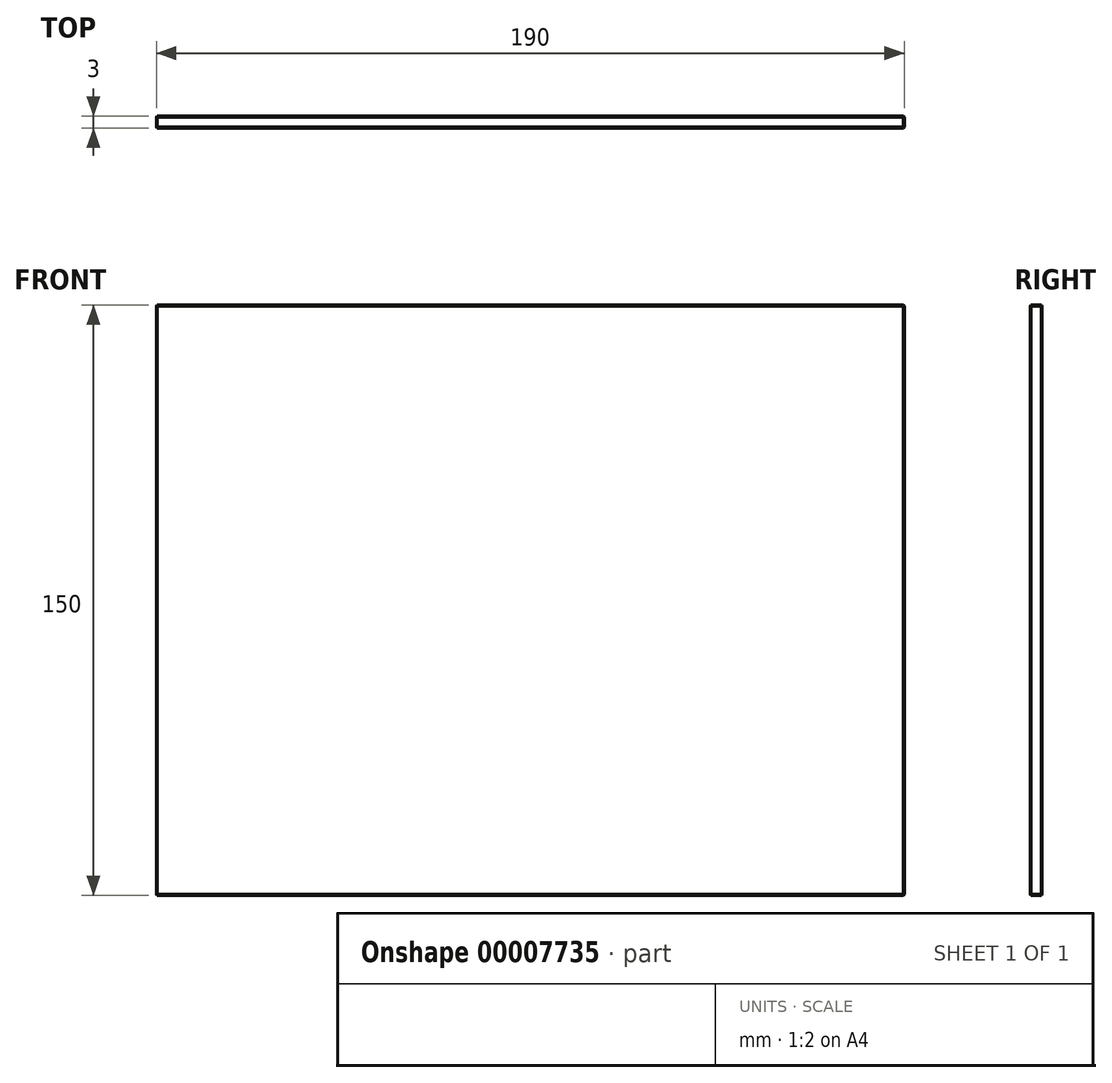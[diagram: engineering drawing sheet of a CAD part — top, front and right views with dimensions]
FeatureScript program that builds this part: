
annotation { "Feature Type Name" : "Feature", "Feature Type Description" : "" }
export const myFeature = defineFeature(function(context is Context, id is Id, definition is map)
    precondition{}
    {
        {
            var Q0;
            Q0=qCreatedBy(makeId("Front.planeOp"),FACE);
            var sketch = newSketch(context, id + "F0", { "sketchPlane" : qUnion([Q0])});
            skLineSegment(sketch, "E0.bottom", {"start": v(0, 0) * mm, "end": v(190, 0) * mm});
            skLineSegment(sketch, "E0.top", {"start": v(0, 150) * mm, "end": v(190, 150) * mm});
            skLineSegment(sketch, "E0.left", {"start": v(0, 0) * mm, "end": v(0, 150) * mm});
            skLineSegment(sketch, "E0.right", {"start": v(190, 0) * mm, "end": v(190, 150) * mm});
            skSolve(sketch);
        }
        {
            var Q0;
            Q0=makeQuery(id+"F0.imprint","IMPRINT",FACE,{"disambiguationData":[TD([[makeQuery(id+"F0.imprint","IMPRINT",EDGE,{"derivedFrom":sQuery(id+"F0.wireOp",EDGE,"E0.bottom")}),1.0]])]});
            extrude(context, id + "F1", {"entities" : qUnion([Q0]), "depth" : 3 * mm});
        }
        {
            var Q0;
            Q0=makeQuery(id+"F1.opExtrude","CAP_EDGE",EDGE,{"disambiguationData":[OSD([sQuery(id+"F0.wireOp",EDGE,"E0.left")])],"isStart":false});
            var Q1;
            Q1=makeQuery(id+"F1.opExtrude","SWEPT_FACE",FACE,{"disambiguationData":[OSD([sQuery(id+"F0.wireOp",EDGE,"E0.left")])]});
            var Q2;
            Q2=makeQuery(id+"F1.opExtrude","SWEPT_FACE",FACE,{"disambiguationData":[OSD([sQuery(id+"F0.wireOp",EDGE,"E0.bottom")])]});
            var Q3;
            Q3=makeQuery(id+"F1.opExtrude","CAP_FACE",FACE,{"disambiguationData":[OSD([sQuery(id+"F0.wireOp",EDGE,"E0.bottom"),sQuery(id+"F0.wireOp",EDGE,"E0.top"),sQuery(id+"F0.wireOp",EDGE,"E0.left"),sQuery(id+"F0.wireOp",EDGE,"E0.right")])],"isStart":false});
            var Q4;
            Q4=makeQuery(id+"F1.opExtrude","CAP_FACE",FACE,{"disambiguationData":[OSD([sQuery(id+"F0.wireOp",EDGE,"E0.bottom"),sQuery(id+"F0.wireOp",EDGE,"E0.top"),sQuery(id+"F0.wireOp",EDGE,"E0.left"),sQuery(id+"F0.wireOp",EDGE,"E0.right")])],"isStart":true});
            var Q5;
            Q5=makeQuery(id+"F1.opExtrude","SWEPT_EDGE",EDGE,{"disambiguationData":[OSD([sQuery(id+"F0.wireOp",EDGE,"E0.top"),sQuery(id+"F0.wireOp",EDGE,"E0.right")])]});
            chamfer(context, id + "F2", {"entities" : qUnion([Q0, Q1, Q2, Q3, Q4, Q5]), "width" : .2 * mm, "tangentPropagation" : true});
        }
    });
